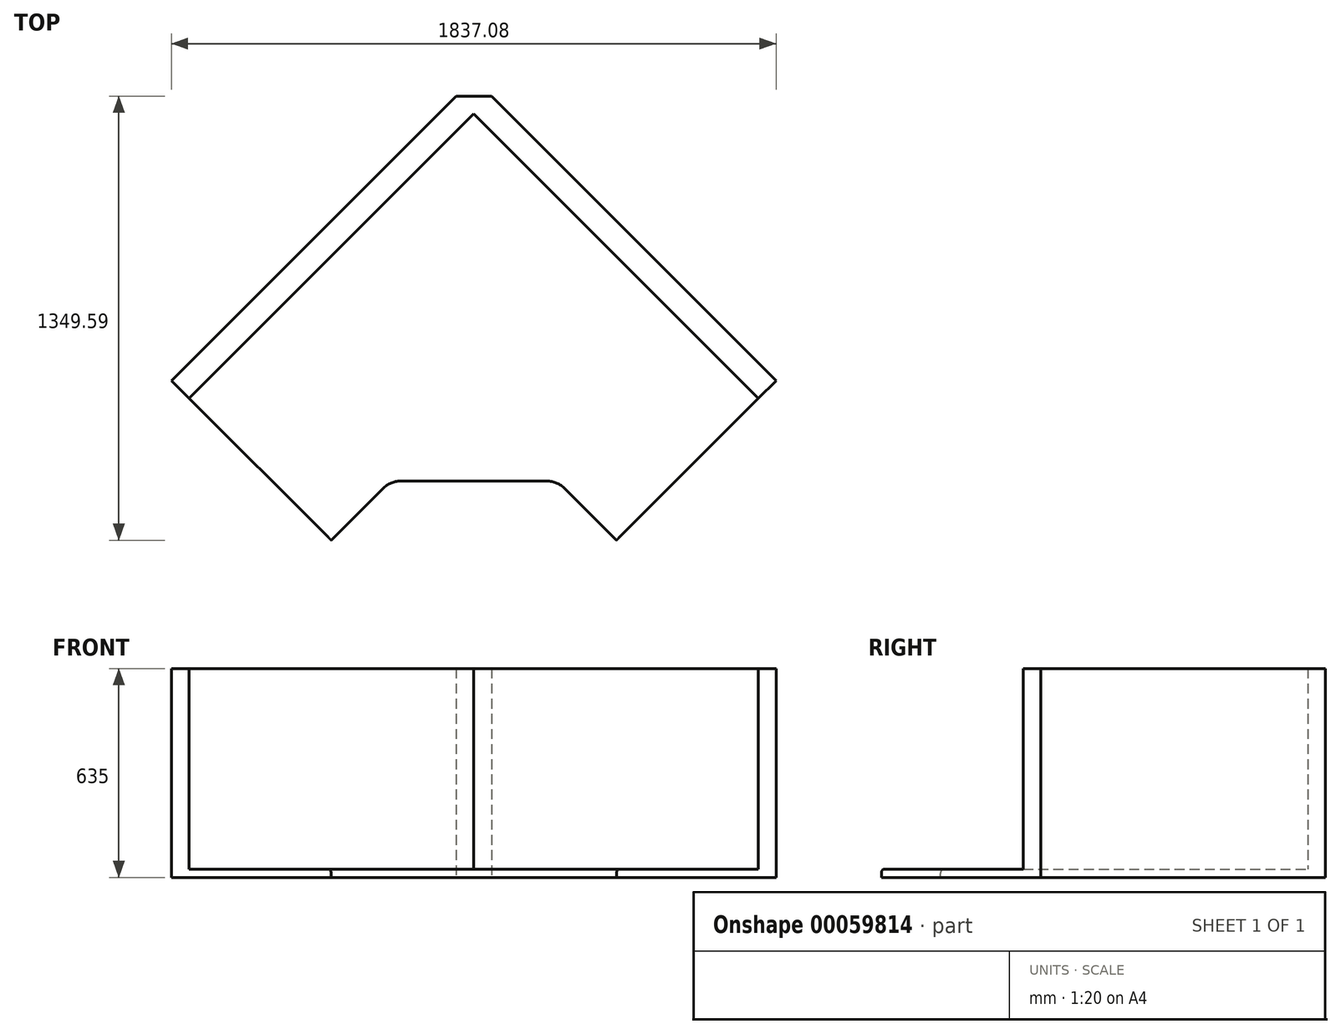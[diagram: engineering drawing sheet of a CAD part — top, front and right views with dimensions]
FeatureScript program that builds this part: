
annotation { "Feature Type Name" : "Feature", "Feature Type Description" : "" }
export const myFeature = defineFeature(function(context is Context, id is Id, definition is map)
    precondition{}
    {
        {
            var Q0;
            Q0=qCreatedBy(makeId("Top.planeOp"),FACE);
            var sketch = newSketch(context, id + "F0", { "sketchPlane" : qUnion([Q0])});
            skLineSegment(sketch, "E0", {"start": v(864.66, -864.66) * mm, "end": v(0, 0) * mm});
            skLineSegment(sketch, "E1", {"start": v(0, 0) * mm, "end": v(-864.66, -864.66) * mm});
            skLineSegment(sketch, "E2", {"start": v(864.66, -864.66) * mm, "end": v(433.6, -1295.7) * mm});
            skLineSegment(sketch, "E3", {"start": v(433.6, -1295.7) * mm, "end": v(254, -1116.1) * mm});
            skLineSegment(sketch, "E4", {"start": v(254, -1116.1) * mm, "end": v(-254, -1116.1) * mm});
            skLineSegment(sketch, "E5", {"start": v(-254, -1116.1) * mm, "end": v(-433.6, -1295.7) * mm});
            skLineSegment(sketch, "E6", {"start": v(-433.6, -1295.7) * mm, "end": v(-864.66, -864.66) * mm});
            skLineSegment(sketch, "E7", {"start": v(864.66, -864.66) * mm, "end": v(918.54, -810.78) * mm});
            skLineSegment(sketch, "E8", {"start": v(918.54, -810.78) * mm, "end": v(53.88, 53.88) * mm});
            skLineSegment(sketch, "E9", {"start": v(53.88, 53.88) * mm, "end": v(0, 0) * mm});
            skLineSegment(sketch, "E10", {"start": v(-864.66, -864.66) * mm, "end": v(-918.54, -810.78) * mm});
            skLineSegment(sketch, "E11", {"start": v(-918.54, -810.78) * mm, "end": v(-53.88, 53.88) * mm});
            skLineSegment(sketch, "E12", {"start": v(-53.88, 53.88) * mm, "end": v(0, 0) * mm});
            skLineSegment(sketch, "E13", {"start": v(-53.88, 53.88) * mm, "end": v(53.88, 53.88) * mm});
            skSolve(sketch);
        }
        {
            var Q0;
            Q0=makeQuery(id+"F0.imprint","IMPRINT",FACE,{"disambiguationData":[TD([[makeQuery(id+"F0.imprint","IMPRINT",EDGE,{"derivedFrom":sQuery(id+"F0.wireOp",EDGE,"E0")}),1.0]])]});
            extrude(context, id + "F1", {"entities" : qUnion([Q0]), "oppositeDirection" : true, "depth" : 25.4 * mm});
        }
        {
            var Q0;
            Q0=makeQuery(id+"F0.imprint","IMPRINT",FACE,{"disambiguationData":[TD([[makeQuery(id+"F0.imprint","IMPRINT",EDGE,{"derivedFrom":sQuery(id+"F0.wireOp",EDGE,"E9")}),-1.0]])]});
            extrude(context, id + "F2", {"entities" : qUnion([Q0]), "depth" : 609.6 * mm, "hasSecondDirection" : true, "secondDirectionOppositeDirection" : true, "secondDirectionDepth" : 25.4 * mm});
        }
        {
            var Q0;
            Q0=makeQuery(id+"F0.imprint","IMPRINT",FACE,{"disambiguationData":[TD([[makeQuery(id+"F0.imprint","IMPRINT",EDGE,{"derivedFrom":sQuery(id+"F0.wireOp",EDGE,"E0")}),-1.0]])]});
            var Q1;
            Q1=makeQuery(id+"F2.opExtrude","CAP_FACE",FACE,{"disambiguationData":[OSD([sQuery(id+"F0.wireOp",EDGE,"E9"),sQuery(id+"F0.wireOp",EDGE,"E12"),sQuery(id+"F0.wireOp",EDGE,"E13")])],"isStart":false});
            extrude(context, id + "F3", {"entities" : qUnion([Q0]), "operationType" : NewBodyOperationType.ADD, "endBound" : BoundingType.UP_TO_SURFACE, "endBoundEntityFace" : qUnion([Q1]), "depth" : 914.4 * mm, "hasSecondDirection" : true, "secondDirectionOppositeDirection" : true, "secondDirectionDepth" : 25.4 * mm});
        }
        {
            var Q0;
            Q0=makeQuery(id+"F0.imprint","IMPRINT",FACE,{"disambiguationData":[TD([[makeQuery(id+"F0.imprint","IMPRINT",EDGE,{"derivedFrom":sQuery(id+"F0.wireOp",EDGE,"E1")}),-1.0]])]});
            var Q1;
            {var subQ0=sQuery(id+"F0.wireOp",EDGE,"E9");Q1=makeQuery(id+"F3.boolean.opBoolean","MERGE",FACE,{"derivedFrom":[makeQuery(id+"F2.opExtrude","CAP_FACE",FACE,{"disambiguationData":[OSD([subQ0,sQuery(id+"F0.wireOp",EDGE,"E12"),sQuery(id+"F0.wireOp",EDGE,"E13")])],"isStart":false}),makeQuery(id+"F3.opExtrude","CAP_FACE",FACE,{"disambiguationData":[OSD([sQuery(id+"F0.wireOp",EDGE,"E0"),sQuery(id+"F0.wireOp",EDGE,"E7"),sQuery(id+"F0.wireOp",EDGE,"E8"),subQ0])],"isStart":false})]});}
            extrude(context, id + "F4", {"entities" : qUnion([Q0]), "operationType" : NewBodyOperationType.ADD, "endBound" : BoundingType.UP_TO_SURFACE, "endBoundEntityFace" : qUnion([Q1]), "depth" : 25.4 * mm, "hasSecondDirection" : true, "secondDirectionOppositeDirection" : true, "secondDirectionDepth" : 25.4 * mm});
        }
        {
            var Q0;
            Q0=makeQuery(id+"F1.opExtrude","SWEPT_EDGE",EDGE,{"disambiguationData":[OSD([sQuery(id+"F0.wireOp",EDGE,"E4"),sQuery(id+"F0.wireOp",EDGE,"E5")])]});
            var Q1;
            Q1=makeQuery(id+"F1.opExtrude","SWEPT_EDGE",EDGE,{"disambiguationData":[OSD([sQuery(id+"F0.wireOp",EDGE,"E3"),sQuery(id+"F0.wireOp",EDGE,"E4")])]});
            fillet(context, id + "F5", {"entities" : qUnion([Q0, Q1]), "radius" : 76.2 * mm, "tangentPropagation" : true, "allowEdgeOverflow" : false});
        }
        {
            var Q0;
            Q0=makeQuery(id+"F1.opExtrude","CAP_EDGE",EDGE,{"disambiguationData":[OSD([sQuery(id+"F0.wireOp",EDGE,"E3")])],"isStart":true});
            fillet(context, id + "F6", {"entities" : qUnion([Q0]), "radius" : 12.7 * mm, "tangentPropagation" : true, "allowEdgeOverflow" : false});
        }
    });
